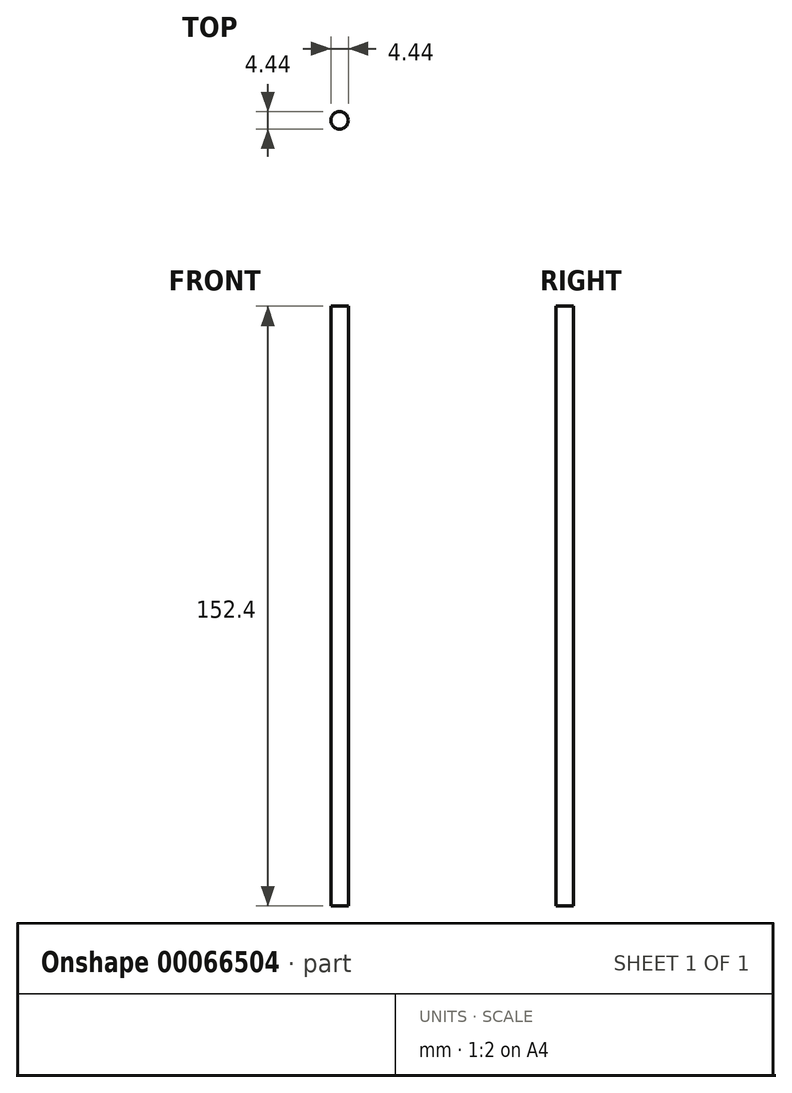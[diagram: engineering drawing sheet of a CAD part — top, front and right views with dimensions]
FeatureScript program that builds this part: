
annotation { "Feature Type Name" : "Feature", "Feature Type Description" : "" }
export const myFeature = defineFeature(function(context is Context, id is Id, definition is map)
    precondition{}
    {
        {
            var Q0;
            Q0=qCreatedBy(makeId("Top.planeOp"),FACE);
            var sketch = newSketch(context, id + "F0", { "sketchPlane" : qUnion([Q0])});
            skCircle(sketch, "E0", {"center": v(0, 0) * mm, "radius": 2.22 * mm});
            skSolve(sketch);
        }
        {
            var Q0;
            Q0=makeQuery(id+"F0.imprint","IMPRINT",FACE,{"disambiguationData":[TD([[makeQuery(id+"F0.imprint","IMPRINT",EDGE,{"derivedFrom":sQuery(id+"F0.wireOp",EDGE,"E0")}),1.0]])]});
            extrude(context, id + "F1", {"entities" : qUnion([Q0]), "depth" : 152.4 * mm});
        }
    });
